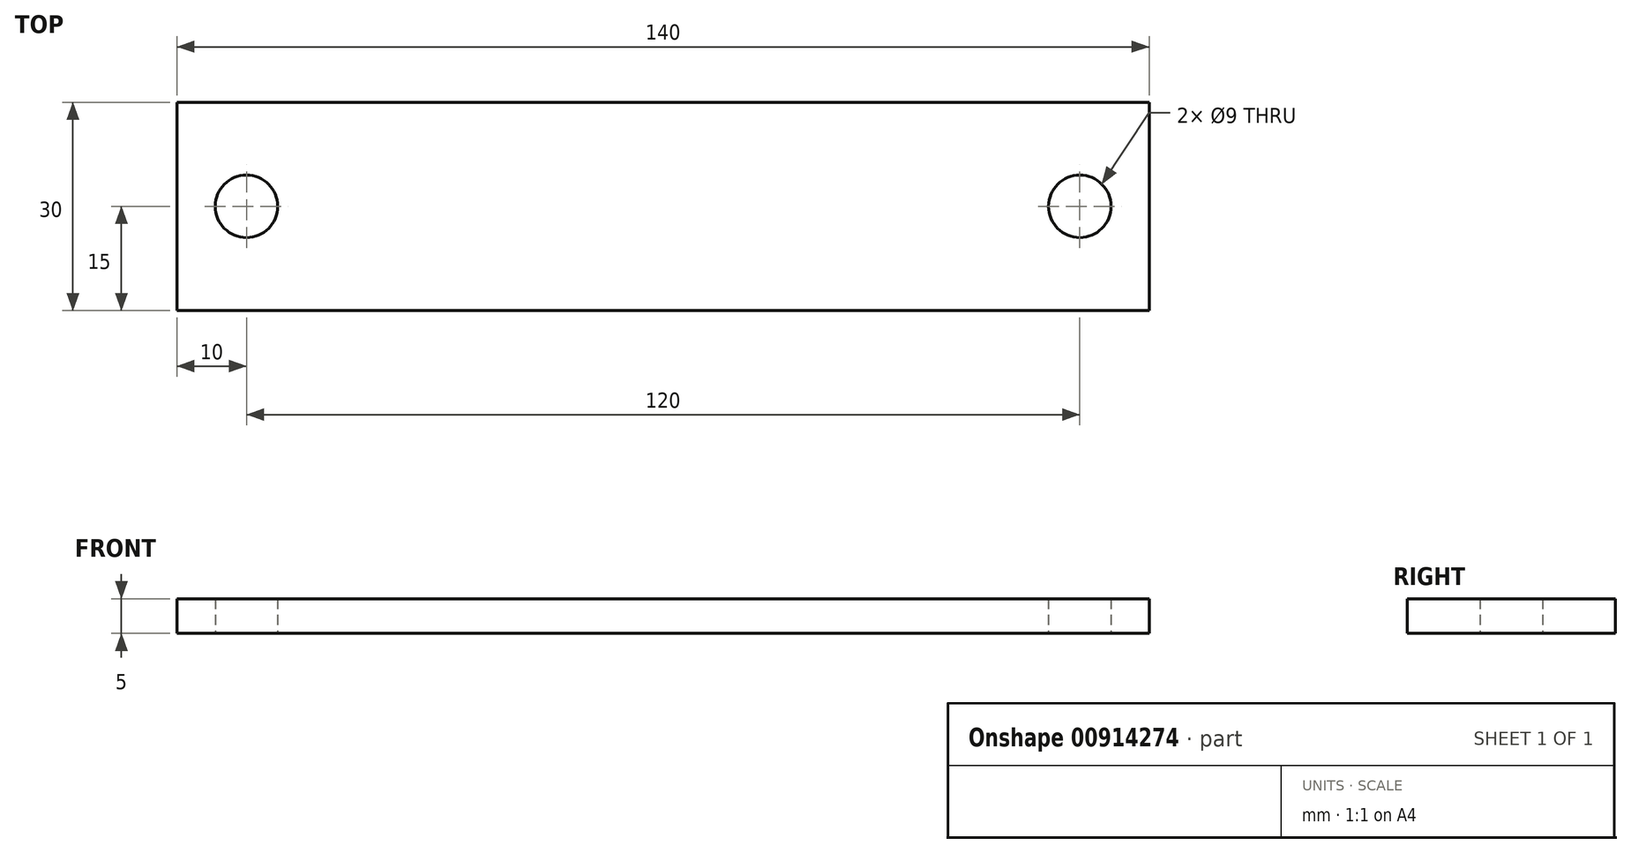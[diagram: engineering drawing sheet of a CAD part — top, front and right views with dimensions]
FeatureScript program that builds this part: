
annotation { "Feature Type Name" : "Feature", "Feature Type Description" : "" }
export const myFeature = defineFeature(function(context is Context, id is Id, definition is map)
    precondition{}
    {
        {
            var Q0;
            Q0=qCreatedBy(makeId("Top.planeOp"),FACE);
            var sketch = newSketch(context, id + "F0", { "sketchPlane" : qUnion([Q0])});
            skLineSegment(sketch, "E0.bottom", {"start": v(70, 15) * mm, "end": v(-70, 15) * mm});
            skLineSegment(sketch, "E0.top", {"start": v(70, -15) * mm, "end": v(-70, -15) * mm});
            skLineSegment(sketch, "E0.left", {"start": v(70, 15) * mm, "end": v(70, -15) * mm});
            skLineSegment(sketch, "E0.right", {"start": v(-70, 15) * mm, "end": v(-70, -15) * mm});
            skPoint(sketch, "E0.middle", {"position": v(0, 0) * mm});
            skCircle(sketch, "E1", {"center": v(-60, 0) * mm, "radius": 4.5 * mm});
            skCircle(sketch, "E2", {"center": v(60, 0) * mm, "radius": 4.5 * mm});
            skSolve(sketch);
        }
        {
            var Q0;
            Q0=makeQuery(id+"F0.imprint","IMPRINT",FACE,{"disambiguationData":[TD([[makeQuery(id+"F0.imprint","IMPRINT",EDGE,{"derivedFrom":sQuery(id+"F0.wireOp",EDGE,"E0.bottom")}),1.0]])]});
            extrude(context, id + "F1", {"entities" : qUnion([Q0]), "depth" : 5 * mm, "offsetDistance" : 25 * mm});
        }
    });
